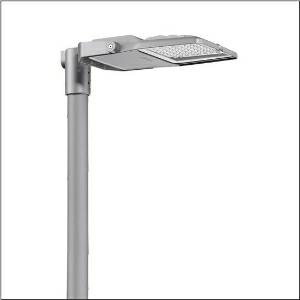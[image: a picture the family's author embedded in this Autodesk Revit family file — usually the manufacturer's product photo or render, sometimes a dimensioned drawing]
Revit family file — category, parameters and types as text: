
# Revit family: floodlight_fl_21_mini___pl61_5xa7776b2c3a_9e12
name_source: partatom
category: Lighting Fixtures
units: mm (PartAtom-declared; Revit-internal decimal feet)

## family parameters
Cut with Voids When Loaded = No
Host = Face
Light Source = No
Part Type = Normal
Room Calculation Point = No
Round Connector Dimension = Use Diameter
Shared = No

## types (1)
- --- (1 x LED, 6110 lm, 45.7 W, 3000K)
    Apparent Load = 46 VA
    CIE Flux Codes = 33 65 98 100 100
    Color Rendering = 70
    Color Temperature = 3000K
    Default Elevation = 1800 mm
    Description = Floodlight FL 21 mini, floodlight, primary light control with lens, of PMMA, primary optical cover: protective disc, of toughened safety glass, transparent, light distribution: PL61, light emission: direct distribution, installation type: surface-mounted, LED, High Power LED, rated luminous flux: 6.110lm, luminous efficacy: 134lm/W, light colour: 730, colour temperature: 3000K, control gear: Smart Interface (Zhaga), control: flexible luminous flux parameterisation, time-dependent luminous flux control, constant luminous flux control, overheat protection, pre-setting: logarithmic dimming characteristic, with terminal, 6-pole, mains connection: 220..240V, AC, 50/60Hz, start of lifetime: 46W, end of service life: 48W, reduction: 22W, luminaire housing, of diecast aluminium, powder-coated, SITECO metallic grey (DB 702S), corrosivity category C5 mid according to DIN EN ISO 12944, suitable for swimming pools, chlorine-resistant, sealing non-destructively replaceable, please order mast flange separately, mast bracket, of steel, galvanised, powder-coated, SITECO metallic grey (DB 702S), Smart Interface below and above, protection rating (complete): IP66, insulation class (complete): insulation class II (safety insulation), certification: CE, ENEC, VDE, protection symbol: D, impact resistance: IK08, permissible operating ambient temperature: -40..+40°C, permissible operating ambient temperature for outdoor applications: -40..+50°C, standard: DIN EN 12944, LABS conformity tested according to VDMA 24364:2018-05, packaging unit: 1 piece

Light Distribution: PL61
    Height = 70 mm
    Lamp = 1 x LED
    Lamp Light Flux = 6110 lm
    Lamp Power = 45.7 W
    Lamp count = 1
    Length = 485 mm
    Luminous efficacy = 134 lm/W
    Manufacturer = Siteco
    ModVariant = No
    Model = 5XA7776B2C3A
    Number of Poles = 1
    OnlyDefault = Yes
    Power Factor = 1
    Product Name = Floodlight FL 21 mini | PL61
    Product group = floodlight | pylon annexe
    ProductGroupID = 6201
    Protection Class = Protection class II
    Protection Degree = IP 66
    RLX_Detail_Level = 1
    RLX_Emergency_Light_Flux = 0 lm
    RLX_Emergency_Type = 0
    RLX_Emergency_Type_DB = No
    RlxData = <blob elided: 101025 chars, md5=b8ea2f4b>
    Socket = socket
    Standby Power = 0 W
    System Light Flux = 6110 lm
    System Power = 46 W
    Type Comments = factory setting: luminous flux: 100 % | dim-lin: 254 | 463 mA
    Type Image = l_1007125.jpg
    URL = http://relux.com
    VarID = @adj_171611
    Voltage = 0 V
    Weight = 0.00 kg
    Width = 337 mm

## geometry (parser evidence)
native form markers: Blend x4, Sweep x13
no freeform markers — native parametric forms only
